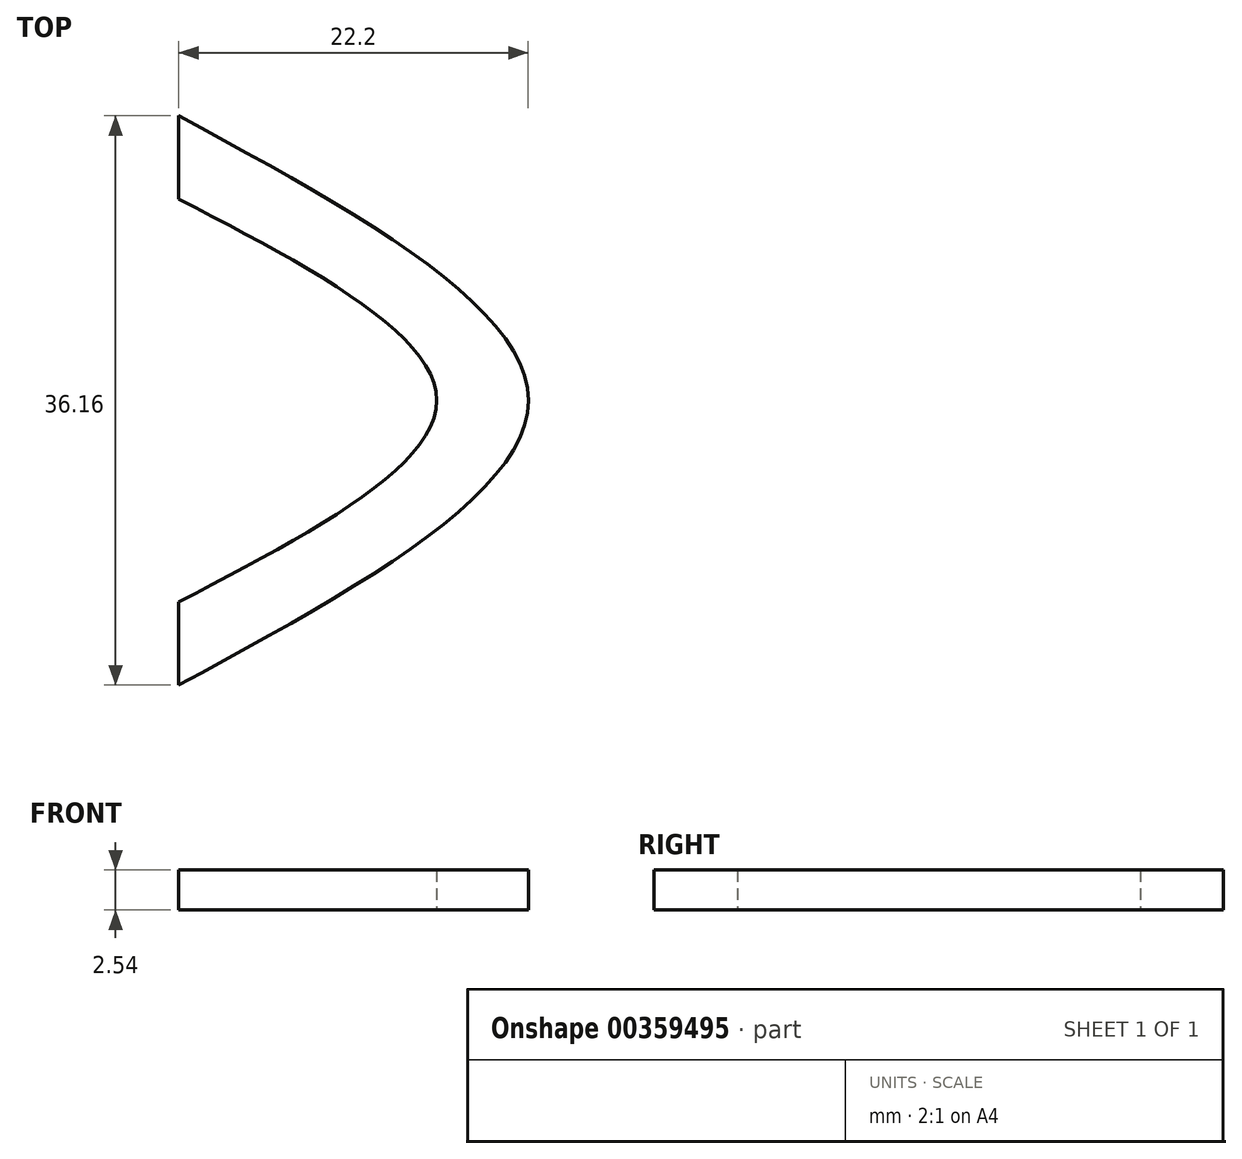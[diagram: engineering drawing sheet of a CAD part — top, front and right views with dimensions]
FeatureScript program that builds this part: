
annotation { "Feature Type Name" : "Feature", "Feature Type Description" : "" }
export const myFeature = defineFeature(function(context is Context, id is Id, definition is map)
    precondition{}
    {
        {
            var Q0;
            Q0=qCreatedBy(makeId("Top.planeOp"),FACE);
            var sketch = newSketch(context, id + "F0", { "sketchPlane" : qUnion([Q0])});
            skPoint(sketch, "E0.1.internal.orphan", {"position": v(16.39, 0) * mm});
            skPoint(sketch, "E0.2.internal.orphan", {"position": v(0, -24.45) * mm});
            skPoint(sketch, "E0.3.internal.orphan", {"position": v(0, -18.08) * mm});
            skLineSegment(sketch, "E1", {"start": v(16.39, 0) * mm, "end": v(22.2, 0) * mm});
            skPoint(sketch, "E2.0.internal.orphan", {"position": v(0, 12.8) * mm});
            skPoint(sketch, "E2.2.internal.orphan", {"position": v(0, -12.8) * mm});
            skPoint(sketch, "E3.2.internal.orphan", {"position": v(0, 18.08) * mm});
            skPoint(sketch, "E3.3.internal.orphan", {"position": v(0, 25.03) * mm});
            skFitSpline(sketch, "E4", {"points": [v(0, -12.8) * mm, v(16.39, 0) * mm, v(0, 12.8) * mm], "startDerivative": vector(49.16, 25.6) * mm, "endDerivative": vector(-49.16, 25.6) * mm});
            skFitSpline(sketch, "E5", {"points": [v(0, -18.08) * mm, v(22.2, 0) * mm, v(0, 18.08) * mm], "startDerivative": vector(66.61, 36.17) * mm, "endDerivative": vector(-66.61, 36.17) * mm});
            skFitSpline(sketch, "E6", {"points": [v(0, -18.08) * mm, v(22.2, 0) * mm, v(0, 18.08) * mm], "startDerivative": vector(66.61, 36.17) * mm, "endDerivative": vector(-66.61, 36.17) * mm});
            skFitSpline(sketch, "E7", {"points": [v(0, -12.8) * mm, v(16.39, 0) * mm, v(0, 12.8) * mm], "startDerivative": vector(49.16, 25.6) * mm, "endDerivative": vector(-49.16, 25.6) * mm});
            skLineSegment(sketch, "E8", {"start": v(0, -12.8) * mm, "end": v(0, -18.08) * mm});
            skLineSegment(sketch, "E9", {"start": v(0, 18.08) * mm, "end": v(0, 12.8) * mm});
            skSolve(sketch);
        }
        {
            var Q0;
            Q0 = qSketchRegion(id + "F0", true);
            extrude(context, id + "F1", {"entities" : qUnion([Q0]), "depth" : 2.54 * mm});
        }
    });
